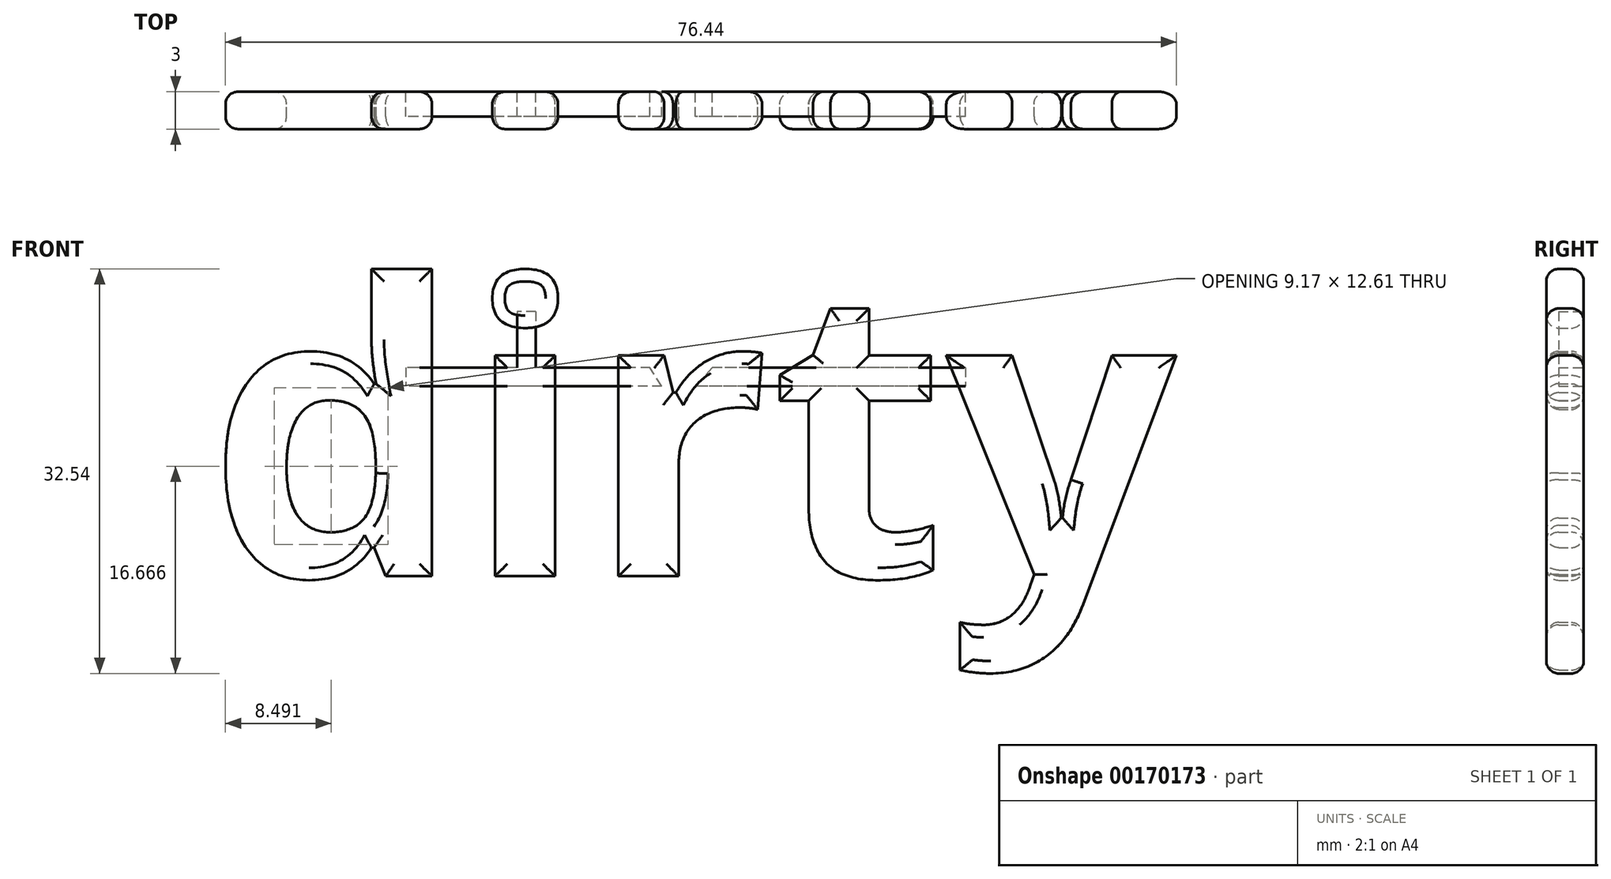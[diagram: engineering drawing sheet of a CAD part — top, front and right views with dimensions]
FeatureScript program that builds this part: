
annotation { "Feature Type Name" : "Feature", "Feature Type Description" : "" }
export const myFeature = defineFeature(function(context is Context, id is Id, definition is map)
    precondition{}
    {
        {
            var Q0;
            Q0=qCreatedBy(makeId("Front.planeOp"),FACE);
            var sketch = newSketch(context, id + "F0", { "sketchPlane" : qUnion([Q0])});
            skText(sketch, "E0", { "text": "dirty", "fontName": "OpenSans-Bold.ttf"});
            const initialGuessF0  = {"E0": [0, 0, 1, 0, 0.02342]};
            skSetInitialGuess(sketch, initialGuessF0);
            skSolve(sketch);
        }
        {
            var Q0;
            Q0 = qSketchRegion(id + "F0", true);
            extrude(context, id + "F1", {"entities" : qUnion([Q0]), "depth" : 3 * mm});
        }
        {
            var Q0;
            Q0=qCreatedBy(makeId("Front.planeOp"),FACE);
            var sketch = newSketch(context, id + "F2", { "sketchPlane" : qUnion([Q0])});
            skLineSegment(sketch, "E1.bottom", {"start": v(60.95, 16.78) * mm, "end": v(40.58, 16.78) * mm});
            skLineSegment(sketch, "E1.top", {"start": v(60.95, 15.28) * mm, "end": v(39.23, 15.28) * mm});
            skLineSegment(sketch, "E1.left", {"start": v(60.95, 16.78) * mm, "end": v(60.95, 15.28) * mm});
            skLineSegment(sketch, "E1.right", {"start": v(15.95, 16.78) * mm, "end": v(15.95, 15.28) * mm});
            skLineSegment(sketch, "E2.bottom", {"start": v(26.4, 21.28) * mm, "end": v(24.9, 21.28) * mm});
            skLineSegment(sketch, "E2.left", {"start": v(26.4, 21.28) * mm, "end": v(26.4, 16.78) * mm});
            skLineSegment(sketch, "E2.right", {"start": v(24.9, 21.28) * mm, "end": v(24.9, 16.78) * mm});
            skLineSegment(sketch, "E3.trimOffspring", {"start": v(24.9, 16.78) * mm, "end": v(15.95, 16.78) * mm});
            skLineSegment(sketch, "E4", {"start": v(40.58, 16.78) * mm, "end": v(39.23, 15.28) * mm});
            skLineSegment(sketch, "E5", {"start": v(36.52, 15.28) * mm, "end": v(35.59, 16.78) * mm});
            skLineSegment(sketch, "E6.trimOffspring", {"start": v(35.59, 16.78) * mm, "end": v(26.4, 16.78) * mm});
            skLineSegment(sketch, "E7.trimOffspring", {"start": v(36.52, 15.28) * mm, "end": v(15.95, 15.28) * mm});
            skSolve(sketch);
        }
        {
            var Q0;
            Q0=makeQuery(id+"F2.imprint","IMPRINT",FACE,{"disambiguationData":[TD([[makeQuery(id+"F2.imprint","IMPRINT",EDGE,{"derivedFrom":sQuery(id+"F2.wireOp",EDGE,"E1.bottom")}),1.0]])]});
            var Q1;
            Q1=makeQuery(id+"F2.imprint","IMPRINT",FACE,{"disambiguationData":[TD([[makeQuery(id+"F2.imprint","IMPRINT",EDGE,{"derivedFrom":sQuery(id+"F2.wireOp",EDGE,"E1.right")}),1.0]])]});
            extrude(context, id + "F3", {"entities" : qUnion([Q0, Q1]), "depth" : 2 * mm});
        }
        {
            var Q0;
            Q0=makeQuery(id+"F1.opExtrude","CAP_FACE",FACE,{"disambiguationData":[OSD([sQuery(id+"F0.wireOp",EDGE,"E0.sketch_text.stroke-0"),sQuery(id+"F0.wireOp",EDGE,"E0.sketch_text.stroke-1"),sQuery(id+"F0.wireOp",EDGE,"E0.sketch_text.stroke-2"),sQuery(id+"F0.wireOp",EDGE,"E0.sketch_text.stroke-3"),sQuery(id+"F0.wireOp",EDGE,"E0.sketch_text.stroke-4"),sQuery(id+"F0.wireOp",EDGE,"E0.sketch_text.stroke-5"),sQuery(id+"F0.wireOp",EDGE,"E0.sketch_text.stroke-6"),sQuery(id+"F0.wireOp",EDGE,"E0.sketch_text.stroke-7"),sQuery(id+"F0.wireOp",EDGE,"E0.sketch_text.stroke-8"),sQuery(id+"F0.wireOp",EDGE,"E0.sketch_text.stroke-9"),sQuery(id+"F0.wireOp",EDGE,"E0.sketch_text.stroke-10"),sQuery(id+"F0.wireOp",EDGE,"E0.sketch_text.stroke-11"),sQuery(id+"F0.wireOp",EDGE,"E0.sketch_text.stroke-12"),sQuery(id+"F0.wireOp",EDGE,"E0.sketch_text.stroke-13"),sQuery(id+"F0.wireOp",EDGE,"E0.sketch_text.stroke-14"),sQuery(id+"F0.wireOp",EDGE,"E0.sketch_text.stroke-15"),sQuery(id+"F0.wireOp",EDGE,"E0.sketch_text.stroke-16"),sQuery(id+"F0.wireOp",EDGE,"E0.sketch_text.stroke-17"),sQuery(id+"F0.wireOp",EDGE,"E0.sketch_text.stroke-18"),sQuery(id+"F0.wireOp",EDGE,"E0.sketch_text.stroke-19"),sQuery(id+"F0.wireOp",EDGE,"E0.sketch_text.stroke-20"),sQuery(id+"F0.wireOp",EDGE,"E0.sketch_text.stroke-21"),sQuery(id+"F0.wireOp",EDGE,"E0.sketch_text.stroke-22")])],"isStart":false});
            var Q1;
            Q1=makeQuery(id+"F1.opExtrude","CAP_FACE",FACE,{"disambiguationData":[OSD([sQuery(id+"F0.wireOp",EDGE,"E0.sketch_text.stroke-28"),sQuery(id+"F0.wireOp",EDGE,"E0.sketch_text.stroke-29"),sQuery(id+"F0.wireOp",EDGE,"E0.sketch_text.stroke-30"),sQuery(id+"F0.wireOp",EDGE,"E0.sketch_text.stroke-31")])],"isStart":false});
            var Q2;
            Q2=makeQuery(id+"F1.opExtrude","CAP_FACE",FACE,{"disambiguationData":[OSD([sQuery(id+"F0.wireOp",EDGE,"E0.sketch_text.stroke-32"),sQuery(id+"F0.wireOp",EDGE,"E0.sketch_text.stroke-33"),sQuery(id+"F0.wireOp",EDGE,"E0.sketch_text.stroke-34"),sQuery(id+"F0.wireOp",EDGE,"E0.sketch_text.stroke-35"),sQuery(id+"F0.wireOp",EDGE,"E0.sketch_text.stroke-36"),sQuery(id+"F0.wireOp",EDGE,"E0.sketch_text.stroke-37"),sQuery(id+"F0.wireOp",EDGE,"E0.sketch_text.stroke-38"),sQuery(id+"F0.wireOp",EDGE,"E0.sketch_text.stroke-39"),sQuery(id+"F0.wireOp",EDGE,"E0.sketch_text.stroke-40"),sQuery(id+"F0.wireOp",EDGE,"E0.sketch_text.stroke-41"),sQuery(id+"F0.wireOp",EDGE,"E0.sketch_text.stroke-42"),sQuery(id+"F0.wireOp",EDGE,"E0.sketch_text.stroke-43"),sQuery(id+"F0.wireOp",EDGE,"E0.sketch_text.stroke-44")])],"isStart":false});
            var Q3;
            Q3=makeQuery(id+"F1.opExtrude","CAP_FACE",FACE,{"disambiguationData":[OSD([sQuery(id+"F0.wireOp",EDGE,"E0.sketch_text.stroke-45"),sQuery(id+"F0.wireOp",EDGE,"E0.sketch_text.stroke-46"),sQuery(id+"F0.wireOp",EDGE,"E0.sketch_text.stroke-47"),sQuery(id+"F0.wireOp",EDGE,"E0.sketch_text.stroke-48"),sQuery(id+"F0.wireOp",EDGE,"E0.sketch_text.stroke-49"),sQuery(id+"F0.wireOp",EDGE,"E0.sketch_text.stroke-50"),sQuery(id+"F0.wireOp",EDGE,"E0.sketch_text.stroke-51"),sQuery(id+"F0.wireOp",EDGE,"E0.sketch_text.stroke-52"),sQuery(id+"F0.wireOp",EDGE,"E0.sketch_text.stroke-53"),sQuery(id+"F0.wireOp",EDGE,"E0.sketch_text.stroke-54"),sQuery(id+"F0.wireOp",EDGE,"E0.sketch_text.stroke-55"),sQuery(id+"F0.wireOp",EDGE,"E0.sketch_text.stroke-56"),sQuery(id+"F0.wireOp",EDGE,"E0.sketch_text.stroke-57"),sQuery(id+"F0.wireOp",EDGE,"E0.sketch_text.stroke-58"),sQuery(id+"F0.wireOp",EDGE,"E0.sketch_text.stroke-59"),sQuery(id+"F0.wireOp",EDGE,"E0.sketch_text.stroke-60"),sQuery(id+"F0.wireOp",EDGE,"E0.sketch_text.stroke-61"),sQuery(id+"F0.wireOp",EDGE,"E0.sketch_text.stroke-62")])],"isStart":false});
            var Q4;
            Q4=makeQuery(id+"F1.opExtrude","CAP_FACE",FACE,{"disambiguationData":[OSD([sQuery(id+"F0.wireOp",EDGE,"E0.sketch_text.stroke-63"),sQuery(id+"F0.wireOp",EDGE,"E0.sketch_text.stroke-64"),sQuery(id+"F0.wireOp",EDGE,"E0.sketch_text.stroke-65"),sQuery(id+"F0.wireOp",EDGE,"E0.sketch_text.stroke-66"),sQuery(id+"F0.wireOp",EDGE,"E0.sketch_text.stroke-67"),sQuery(id+"F0.wireOp",EDGE,"E0.sketch_text.stroke-68"),sQuery(id+"F0.wireOp",EDGE,"E0.sketch_text.stroke-69"),sQuery(id+"F0.wireOp",EDGE,"E0.sketch_text.stroke-70"),sQuery(id+"F0.wireOp",EDGE,"E0.sketch_text.stroke-71"),sQuery(id+"F0.wireOp",EDGE,"E0.sketch_text.stroke-72"),sQuery(id+"F0.wireOp",EDGE,"E0.sketch_text.stroke-73"),sQuery(id+"F0.wireOp",EDGE,"E0.sketch_text.stroke-74"),sQuery(id+"F0.wireOp",EDGE,"E0.sketch_text.stroke-75"),sQuery(id+"F0.wireOp",EDGE,"E0.sketch_text.stroke-76"),sQuery(id+"F0.wireOp",EDGE,"E0.sketch_text.stroke-77"),sQuery(id+"F0.wireOp",EDGE,"E0.sketch_text.stroke-78"),sQuery(id+"F0.wireOp",EDGE,"E0.sketch_text.stroke-79")])],"isStart":false});
            var Q5;
            Q5=makeQuery(id+"F1.opExtrude","CAP_FACE",FACE,{"disambiguationData":[OSD([sQuery(id+"F0.wireOp",EDGE,"E0.sketch_text.stroke-23"),sQuery(id+"F0.wireOp",EDGE,"E0.sketch_text.stroke-24"),sQuery(id+"F0.wireOp",EDGE,"E0.sketch_text.stroke-25"),sQuery(id+"F0.wireOp",EDGE,"E0.sketch_text.stroke-26"),sQuery(id+"F0.wireOp",EDGE,"E0.sketch_text.stroke-27")])],"isStart":false});
            var Q6;
            Q6=makeQuery(id+"F1.opExtrude","CAP_FACE",FACE,{"disambiguationData":[OSD([sQuery(id+"F0.wireOp",EDGE,"E0.sketch_text.stroke-0"),sQuery(id+"F0.wireOp",EDGE,"E0.sketch_text.stroke-1"),sQuery(id+"F0.wireOp",EDGE,"E0.sketch_text.stroke-2"),sQuery(id+"F0.wireOp",EDGE,"E0.sketch_text.stroke-3"),sQuery(id+"F0.wireOp",EDGE,"E0.sketch_text.stroke-4"),sQuery(id+"F0.wireOp",EDGE,"E0.sketch_text.stroke-5"),sQuery(id+"F0.wireOp",EDGE,"E0.sketch_text.stroke-6"),sQuery(id+"F0.wireOp",EDGE,"E0.sketch_text.stroke-7"),sQuery(id+"F0.wireOp",EDGE,"E0.sketch_text.stroke-8"),sQuery(id+"F0.wireOp",EDGE,"E0.sketch_text.stroke-9"),sQuery(id+"F0.wireOp",EDGE,"E0.sketch_text.stroke-10"),sQuery(id+"F0.wireOp",EDGE,"E0.sketch_text.stroke-11"),sQuery(id+"F0.wireOp",EDGE,"E0.sketch_text.stroke-12"),sQuery(id+"F0.wireOp",EDGE,"E0.sketch_text.stroke-13"),sQuery(id+"F0.wireOp",EDGE,"E0.sketch_text.stroke-14"),sQuery(id+"F0.wireOp",EDGE,"E0.sketch_text.stroke-15"),sQuery(id+"F0.wireOp",EDGE,"E0.sketch_text.stroke-16"),sQuery(id+"F0.wireOp",EDGE,"E0.sketch_text.stroke-17"),sQuery(id+"F0.wireOp",EDGE,"E0.sketch_text.stroke-18"),sQuery(id+"F0.wireOp",EDGE,"E0.sketch_text.stroke-19"),sQuery(id+"F0.wireOp",EDGE,"E0.sketch_text.stroke-20"),sQuery(id+"F0.wireOp",EDGE,"E0.sketch_text.stroke-21"),sQuery(id+"F0.wireOp",EDGE,"E0.sketch_text.stroke-22")])],"isStart":true});
            var Q7;
            Q7=makeQuery(id+"F1.opExtrude","CAP_FACE",FACE,{"disambiguationData":[OSD([sQuery(id+"F0.wireOp",EDGE,"E0.sketch_text.stroke-28"),sQuery(id+"F0.wireOp",EDGE,"E0.sketch_text.stroke-29"),sQuery(id+"F0.wireOp",EDGE,"E0.sketch_text.stroke-30"),sQuery(id+"F0.wireOp",EDGE,"E0.sketch_text.stroke-31")])],"isStart":true});
            var Q8;
            Q8=makeQuery(id+"F1.opExtrude","CAP_FACE",FACE,{"disambiguationData":[OSD([sQuery(id+"F0.wireOp",EDGE,"E0.sketch_text.stroke-23"),sQuery(id+"F0.wireOp",EDGE,"E0.sketch_text.stroke-24"),sQuery(id+"F0.wireOp",EDGE,"E0.sketch_text.stroke-25"),sQuery(id+"F0.wireOp",EDGE,"E0.sketch_text.stroke-26"),sQuery(id+"F0.wireOp",EDGE,"E0.sketch_text.stroke-27")])],"isStart":true});
            var Q9;
            Q9=makeQuery(id+"F1.opExtrude","CAP_FACE",FACE,{"disambiguationData":[OSD([sQuery(id+"F0.wireOp",EDGE,"E0.sketch_text.stroke-32"),sQuery(id+"F0.wireOp",EDGE,"E0.sketch_text.stroke-33"),sQuery(id+"F0.wireOp",EDGE,"E0.sketch_text.stroke-34"),sQuery(id+"F0.wireOp",EDGE,"E0.sketch_text.stroke-35"),sQuery(id+"F0.wireOp",EDGE,"E0.sketch_text.stroke-36"),sQuery(id+"F0.wireOp",EDGE,"E0.sketch_text.stroke-37"),sQuery(id+"F0.wireOp",EDGE,"E0.sketch_text.stroke-38"),sQuery(id+"F0.wireOp",EDGE,"E0.sketch_text.stroke-39"),sQuery(id+"F0.wireOp",EDGE,"E0.sketch_text.stroke-40"),sQuery(id+"F0.wireOp",EDGE,"E0.sketch_text.stroke-41"),sQuery(id+"F0.wireOp",EDGE,"E0.sketch_text.stroke-42"),sQuery(id+"F0.wireOp",EDGE,"E0.sketch_text.stroke-43"),sQuery(id+"F0.wireOp",EDGE,"E0.sketch_text.stroke-44")])],"isStart":true});
            var Q10;
            Q10=makeQuery(id+"F1.opExtrude","CAP_FACE",FACE,{"disambiguationData":[OSD([sQuery(id+"F0.wireOp",EDGE,"E0.sketch_text.stroke-45"),sQuery(id+"F0.wireOp",EDGE,"E0.sketch_text.stroke-46"),sQuery(id+"F0.wireOp",EDGE,"E0.sketch_text.stroke-47"),sQuery(id+"F0.wireOp",EDGE,"E0.sketch_text.stroke-48"),sQuery(id+"F0.wireOp",EDGE,"E0.sketch_text.stroke-49"),sQuery(id+"F0.wireOp",EDGE,"E0.sketch_text.stroke-50"),sQuery(id+"F0.wireOp",EDGE,"E0.sketch_text.stroke-51"),sQuery(id+"F0.wireOp",EDGE,"E0.sketch_text.stroke-52"),sQuery(id+"F0.wireOp",EDGE,"E0.sketch_text.stroke-53"),sQuery(id+"F0.wireOp",EDGE,"E0.sketch_text.stroke-54"),sQuery(id+"F0.wireOp",EDGE,"E0.sketch_text.stroke-55"),sQuery(id+"F0.wireOp",EDGE,"E0.sketch_text.stroke-56"),sQuery(id+"F0.wireOp",EDGE,"E0.sketch_text.stroke-57"),sQuery(id+"F0.wireOp",EDGE,"E0.sketch_text.stroke-58"),sQuery(id+"F0.wireOp",EDGE,"E0.sketch_text.stroke-59"),sQuery(id+"F0.wireOp",EDGE,"E0.sketch_text.stroke-60"),sQuery(id+"F0.wireOp",EDGE,"E0.sketch_text.stroke-61"),sQuery(id+"F0.wireOp",EDGE,"E0.sketch_text.stroke-62")])],"isStart":true});
            var Q11;
            Q11=makeQuery(id+"F1.opExtrude","CAP_FACE",FACE,{"disambiguationData":[OSD([sQuery(id+"F0.wireOp",EDGE,"E0.sketch_text.stroke-63"),sQuery(id+"F0.wireOp",EDGE,"E0.sketch_text.stroke-64"),sQuery(id+"F0.wireOp",EDGE,"E0.sketch_text.stroke-65"),sQuery(id+"F0.wireOp",EDGE,"E0.sketch_text.stroke-66"),sQuery(id+"F0.wireOp",EDGE,"E0.sketch_text.stroke-67"),sQuery(id+"F0.wireOp",EDGE,"E0.sketch_text.stroke-68"),sQuery(id+"F0.wireOp",EDGE,"E0.sketch_text.stroke-69"),sQuery(id+"F0.wireOp",EDGE,"E0.sketch_text.stroke-70"),sQuery(id+"F0.wireOp",EDGE,"E0.sketch_text.stroke-71"),sQuery(id+"F0.wireOp",EDGE,"E0.sketch_text.stroke-72"),sQuery(id+"F0.wireOp",EDGE,"E0.sketch_text.stroke-73"),sQuery(id+"F0.wireOp",EDGE,"E0.sketch_text.stroke-74"),sQuery(id+"F0.wireOp",EDGE,"E0.sketch_text.stroke-75"),sQuery(id+"F0.wireOp",EDGE,"E0.sketch_text.stroke-76"),sQuery(id+"F0.wireOp",EDGE,"E0.sketch_text.stroke-77"),sQuery(id+"F0.wireOp",EDGE,"E0.sketch_text.stroke-78"),sQuery(id+"F0.wireOp",EDGE,"E0.sketch_text.stroke-79")])],"isStart":true});
            fillet(context, id + "F4", {"entities" : qUnion([Q0, Q1, Q2, Q3, Q4, Q5, Q6, Q7, Q8, Q9, Q10, Q11]), "radius" : 1 * mm, "tangentPropagation" : true, "allowEdgeOverflow" : false});
        }
    });
